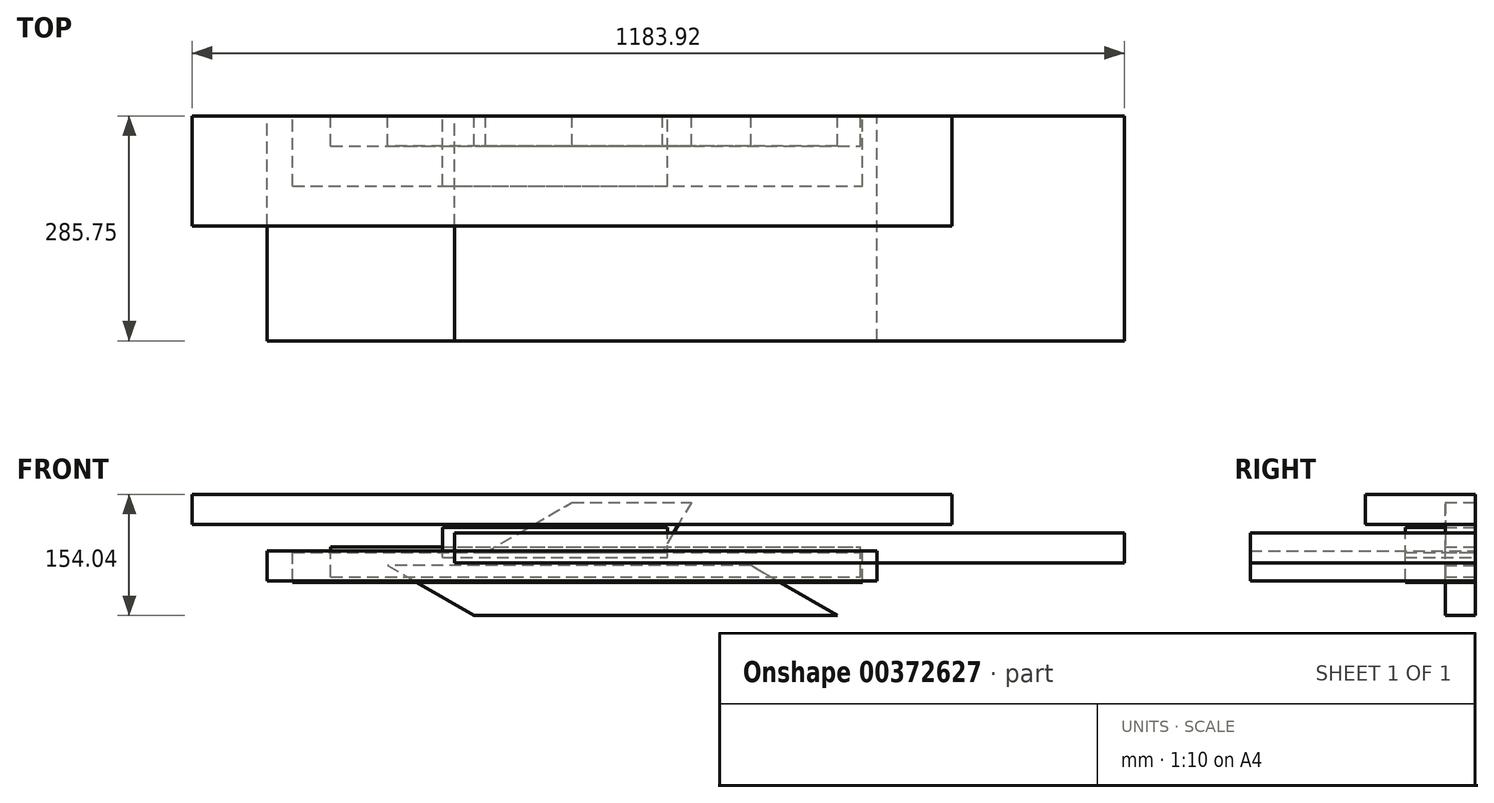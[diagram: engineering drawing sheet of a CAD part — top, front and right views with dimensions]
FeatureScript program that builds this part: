
annotation { "Feature Type Name" : "Feature", "Feature Type Description" : "" }
export const myFeature = defineFeature(function(context is Context, id is Id, definition is map)
    precondition{}
    {
        {
            var Q0;
            Q0=qCreatedBy(makeId("Front.planeOp"),FACE);
            var sketch = newSketch(context, id + "F0", { "sketchPlane" : qUnion([Q0])});
            skLineSegment(sketch, "E0.bottom", {"start": v(482.6, 0) * mm, "end": v(-482.6, 0) * mm});
            skLineSegment(sketch, "E0.top", {"start": v(482.6, 38.1) * mm, "end": v(-482.6, 38.1) * mm});
            skLineSegment(sketch, "E0.left", {"start": v(482.6, 0) * mm, "end": v(482.6, 38.1) * mm});
            skLineSegment(sketch, "E0.right", {"start": v(-482.6, 0) * mm, "end": v(-482.6, 38.1) * mm});
            skPoint(sketch, "E0.middle", {"position": v(0, 19.05) * mm});
            skSolve(sketch);
        }
        {
            var Q0;
            Q0 = qSketchRegion(id + "F0", true);
            extrude(context, id + "F1", {"entities" : qUnion([Q0]), "depth" : 139.7 * mm});
        }
        {
            var Q0;
            Q0=makeQuery(id+"F1.opExtrude","SWEPT_BODY",BODY,{"disambiguationData":[OSD([sQuery(id+"F0.wireOp",EDGE,"E0.bottom"),sQuery(id+"F0.wireOp",EDGE,"E0.top"),sQuery(id+"F0.wireOp",EDGE,"E0.left"),sQuery(id+"F0.wireOp",EDGE,"E0.right")])]});
            transform(context, id + "F2", {"entities" : qUnion([Q0]), "transformType" : TransformType.TRANSLATION_3D, "dx" : 0 * mm, "dy" : 0 * mm, "dz" : 0 * mm, "makeCopy" : true});
        }
        {
            var Q0;
            Q0=makeQuery(id+"F2.opPattern","COPY",BODY,{"derivedFrom":makeQuery(id+"F1.opExtrude","SWEPT_BODY",BODY,{"disambiguationData":[OSD([sQuery(id+"F0.wireOp",EDGE,"E0.bottom"),sQuery(id+"F0.wireOp",EDGE,"E0.top"),sQuery(id+"F0.wireOp",EDGE,"E0.left"),sQuery(id+"F0.wireOp",EDGE,"E0.right")])]}),"instanceName":"1"});
            deleteBodies(context, id + "F3", {"entities" : qUnion([Q0])});
        }
        {
            var Q0;
            Q0=makeQuery(id+"F1.opExtrude","SWEPT_BODY",BODY,{"disambiguationData":[OSD([sQuery(id+"F0.wireOp",EDGE,"E0.bottom"),sQuery(id+"F0.wireOp",EDGE,"E0.top"),sQuery(id+"F0.wireOp",EDGE,"E0.left"),sQuery(id+"F0.wireOp",EDGE,"E0.right")])]});
            transform(context, id + "F4", {"entities" : qUnion([Q0]), "transformType" : TransformType.TRANSLATION_3D, "dx" : 0 * mm, "dy" : 0 * mm, "dz" : 0 * mm, "makeCopy" : true});
        }
        {
            var Q0;
            Q0=makeQuery(id+"F4.opPattern","COPY",BODY,{"derivedFrom":makeQuery(id+"F1.opExtrude","SWEPT_BODY",BODY,{"disambiguationData":[OSD([sQuery(id+"F0.wireOp",EDGE,"E0.bottom"),sQuery(id+"F0.wireOp",EDGE,"E0.top"),sQuery(id+"F0.wireOp",EDGE,"E0.left"),sQuery(id+"F0.wireOp",EDGE,"E0.right")])]}),"instanceName":"1"});
            transform(context, id + "F5", {"entities" : qUnion([Q0]), "transformType" : TransformType.TRANSLATION_3D, "dx" : 0 * mm, "dy" : 0 * mm, "dz" : 0 * mm, "makeCopy" : true});
        }
        {
            var Q0;
            Q0=makeQuery(id+"F5.opPattern","COPY",BODY,{"derivedFrom":makeQuery(id+"F4.opPattern","COPY",BODY,{"derivedFrom":makeQuery(id+"F1.opExtrude","SWEPT_BODY",BODY,{"disambiguationData":[OSD([sQuery(id+"F0.wireOp",EDGE,"E0.bottom"),sQuery(id+"F0.wireOp",EDGE,"E0.top"),sQuery(id+"F0.wireOp",EDGE,"E0.left"),sQuery(id+"F0.wireOp",EDGE,"E0.right")])]}),"instanceName":"1"}),"instanceName":"1"});
            transform(context, id + "F6", {"entities" : qUnion([Q0]), "transformType" : TransformType.TRANSLATION_3D, "dx" : 0 * mm, "dy" : 0 * mm, "dz" : 0 * mm, "makeCopy" : true});
        }
        {
            var Q0;
            Q0=makeQuery(id+"F4.opPattern","COPY",BODY,{"derivedFrom":makeQuery(id+"F1.opExtrude","SWEPT_BODY",BODY,{"disambiguationData":[OSD([sQuery(id+"F0.wireOp",EDGE,"E0.bottom"),sQuery(id+"F0.wireOp",EDGE,"E0.top"),sQuery(id+"F0.wireOp",EDGE,"E0.left"),sQuery(id+"F0.wireOp",EDGE,"E0.right")])]}),"instanceName":"1"});
            deleteBodies(context, id + "F7", {"entities" : qUnion([Q0])});
        }
        {
            var Q0;
            Q0=makeQuery(id+"F5.opPattern","COPY",BODY,{"derivedFrom":makeQuery(id+"F4.opPattern","COPY",BODY,{"derivedFrom":makeQuery(id+"F1.opExtrude","SWEPT_BODY",BODY,{"disambiguationData":[OSD([sQuery(id+"F0.wireOp",EDGE,"E0.bottom"),sQuery(id+"F0.wireOp",EDGE,"E0.top"),sQuery(id+"F0.wireOp",EDGE,"E0.left"),sQuery(id+"F0.wireOp",EDGE,"E0.right")])]}),"instanceName":"1"}),"instanceName":"1"});
            deleteBodies(context, id + "F8", {"entities" : qUnion([Q0])});
        }
        {
            var Q0;
            Q0=makeQuery(id+"F6.opPattern","COPY",BODY,{"derivedFrom":makeQuery(id+"F5.opPattern","COPY",BODY,{"derivedFrom":makeQuery(id+"F4.opPattern","COPY",BODY,{"derivedFrom":makeQuery(id+"F1.opExtrude","SWEPT_BODY",BODY,{"disambiguationData":[OSD([sQuery(id+"F0.wireOp",EDGE,"E0.bottom"),sQuery(id+"F0.wireOp",EDGE,"E0.top"),sQuery(id+"F0.wireOp",EDGE,"E0.left"),sQuery(id+"F0.wireOp",EDGE,"E0.right")])]}),"instanceName":"1"}),"instanceName":"1"}),"instanceName":"1"});
            deleteBodies(context, id + "F9", {"entities" : qUnion([Q0])});
        }
        {
            var Q0;
            Q0=qCreatedBy(makeId("Front.planeOp"),FACE);
            var sketch = newSketch(context, id + "F10", { "sketchPlane" : qUnion([Q0])});
            skLineSegment(sketch, "E1.bottom", {"start": v(-355.18, -73.61) * mm, "end": v(368.72, -73.61) * mm});
            skLineSegment(sketch, "E1.top", {"start": v(-355.18, -35.51) * mm, "end": v(368.72, -35.51) * mm});
            skLineSegment(sketch, "E1.left", {"start": v(-355.18, -73.61) * mm, "end": v(-355.18, -35.51) * mm});
            skLineSegment(sketch, "E1.right", {"start": v(368.72, -73.61) * mm, "end": v(368.72, -35.51) * mm});
            skSolve(sketch);
        }
        {
            var Q0;
            Q0 = qSketchRegion(id + "F10", true);
            extrude(context, id + "F11", {"entities" : qUnion([Q0]), "depth" : 88.9 * mm});
        }
        {
            var Q0;
            Q0=qCreatedBy(makeId("Front.planeOp"),FACE);
            var sketch = newSketch(context, id + "F12", { "sketchPlane" : qUnion([Q0])});
            skLineSegment(sketch, "E2.bottom", {"start": v(-149.58, -49.23) * mm, "end": v(701.32, -49.23) * mm});
            skLineSegment(sketch, "E2.top", {"start": v(-149.58, -11.13) * mm, "end": v(701.32, -11.13) * mm});
            skLineSegment(sketch, "E2.left", {"start": v(-149.58, -49.23) * mm, "end": v(-149.58, -11.13) * mm});
            skLineSegment(sketch, "E2.right", {"start": v(701.32, -49.23) * mm, "end": v(701.32, -11.13) * mm});
            skSolve(sketch);
        }
        {
            var Q0;
            Q0 = qSketchRegion(id + "F12", true);
            extrude(context, id + "F13", {"entities" : qUnion([Q0]), "depth" : 285.75 * mm});
        }
        {
            var Q0;
            Q0=qCreatedBy(makeId("Front.planeOp"),FACE);
            var sketch = newSketch(context, id + "F14", { "sketchPlane" : qUnion([Q0])});
            skLineSegment(sketch, "E3.bottom", {"start": v(-387.76, -71.85) * mm, "end": v(386.94, -71.85) * mm});
            skLineSegment(sketch, "E3.top", {"start": v(-387.76, -33.75) * mm, "end": v(386.94, -33.75) * mm});
            skLineSegment(sketch, "E3.left", {"start": v(-387.76, -71.85) * mm, "end": v(-387.76, -33.75) * mm});
            skLineSegment(sketch, "E3.right", {"start": v(386.94, -71.85) * mm, "end": v(386.94, -33.75) * mm});
            skSolve(sketch);
        }
        {
            var Q0;
            Q0 = qSketchRegion(id + "F14", true);
            extrude(context, id + "F15", {"entities" : qUnion([Q0]), "depth" : 285.75 * mm});
        }
        {
            var Q0;
            Q0=qCreatedBy(makeId("Front.planeOp"),FACE);
            var sketch = newSketch(context, id + "F16", { "sketchPlane" : qUnion([Q0])});
            skLineSegment(sketch, "E4.bottom", {"start": v(-164.57, -41.77) * mm, "end": v(121.18, -41.77) * mm});
            skLineSegment(sketch, "E4.top", {"start": v(-164.57, -3.67) * mm, "end": v(121.18, -3.67) * mm});
            skLineSegment(sketch, "E4.left", {"start": v(-164.57, -41.77) * mm, "end": v(-164.57, -3.67) * mm});
            skLineSegment(sketch, "E4.right", {"start": v(121.18, -41.77) * mm, "end": v(121.18, -3.67) * mm});
            skSolve(sketch);
        }
        {
            var Q0;
            Q0 = qSketchRegion(id + "F16", true);
            extrude(context, id + "F17", {"entities" : qUnion([Q0]), "depth" : 88.9 * mm});
        }
        {
            var Q0;
            Q0=qCreatedBy(makeId("Front.planeOp"),FACE);
            var sketch = newSketch(context, id + "F18", { "sketchPlane" : qUnion([Q0])});
            skLineSegment(sketch, "E5.bottom", {"start": v(-306.67, -66.82) * mm, "end": v(366.43, -66.82) * mm});
            skLineSegment(sketch, "E5.top", {"start": v(-306.67, -28.72) * mm, "end": v(366.43, -28.72) * mm});
            skLineSegment(sketch, "E5.left", {"start": v(-306.67, -66.82) * mm, "end": v(-306.67, -28.72) * mm});
            skLineSegment(sketch, "E5.right", {"start": v(366.43, -66.82) * mm, "end": v(366.43, -28.72) * mm});
            skSolve(sketch);
        }
        {
            var Q0;
            Q0 = qSketchRegion(id + "F18", true);
            extrude(context, id + "F19", {"entities" : qUnion([Q0]), "depth" : 38.1 * mm});
        }
        {
            var Q0;
            Q0=qCreatedBy(makeId("Front.planeOp"),FACE);
            var sketch = newSketch(context, id + "F20", { "sketchPlane" : qUnion([Q0])});
            skLineSegment(sketch, "E6.bottom", {"start": v(-109.99, -35.55) * mm, "end": v(114.6, -35.55) * mm});
            skLineSegment(sketch, "E6.top", {"start": v(0, 27.95) * mm, "end": v(151.27, 27.95) * mm});
            skLineSegment(sketch, "E7", {"start": v(-109.99, -35.55) * mm, "end": v(0, 27.95) * mm});
            skLineSegment(sketch, "E8", {"start": v(151.27, 27.95) * mm, "end": v(114.6, -35.55) * mm});
            skSolve(sketch);
        }
        {
            var Q0;
            Q0 = qSketchRegion(id + "F20", true);
            extrude(context, id + "F21", {"entities" : qUnion([Q0]), "depth" : 38.1 * mm});
        }
        {
            var Q0;
            Q0=makeQuery(id+"F21.opExtrude","SWEPT_BODY",BODY,{"disambiguationData":[OSD([sQuery(id+"F20.wireOp",EDGE,"E6.bottom"),sQuery(id+"F20.wireOp",EDGE,"E6.top"),sQuery(id+"F20.wireOp",EDGE,"E7"),sQuery(id+"F20.wireOp",EDGE,"E8")])]});
            transform(context, id + "F22", {"entities" : qUnion([Q0]), "transformType" : TransformType.TRANSLATION_3D, "dx" : 0 * mm, "dy" : 0 * mm, "dz" : 0 * mm, "makeCopy" : true});
        }
        {
            var Q0;
            Q0=makeQuery(id+"F21.opExtrude","SWEPT_BODY",BODY,{"disambiguationData":[OSD([sQuery(id+"F20.wireOp",EDGE,"E6.bottom"),sQuery(id+"F20.wireOp",EDGE,"E6.top"),sQuery(id+"F20.wireOp",EDGE,"E7"),sQuery(id+"F20.wireOp",EDGE,"E8")])]});
            deleteBodies(context, id + "F23", {"entities" : qUnion([Q0])});
        }
        {
            var Q0;
            Q0=qCreatedBy(makeId("Front.planeOp"),FACE);
            var sketch = newSketch(context, id + "F24", { "sketchPlane" : qUnion([Q0])});
            skLineSegment(sketch, "E9.bottom", {"start": v(337.1, -115.94) * mm, "end": v(-124.42, -115.94) * mm});
            skLineSegment(sketch, "E9.top", {"start": v(227.1, -52.44) * mm, "end": v(-234.4, -52.44) * mm});
            skPoint(sketch, "E9.middle", {"position": v(51.34, -84.19) * mm});
            skLineSegment(sketch, "E10", {"start": v(-234.4, -52.44) * mm, "end": v(-124.42, -115.94) * mm});
            skLineSegment(sketch, "E11", {"start": v(337.1, -115.94) * mm, "end": v(227.1, -52.44) * mm});
            skPoint(sketch, "E9.right.start.orphan", {"position": v(-234.4, -115.94) * mm});
            skPoint(sketch, "E9.left.end.orphan", {"position": v(337.1, -52.44) * mm});
            skSolve(sketch);
        }
        {
            var Q0;
            Q0 = qSketchRegion(id + "F24", true);
            extrude(context, id + "F25", {"entities" : qUnion([Q0]), "depth" : 38.1 * mm});
        }
    });
